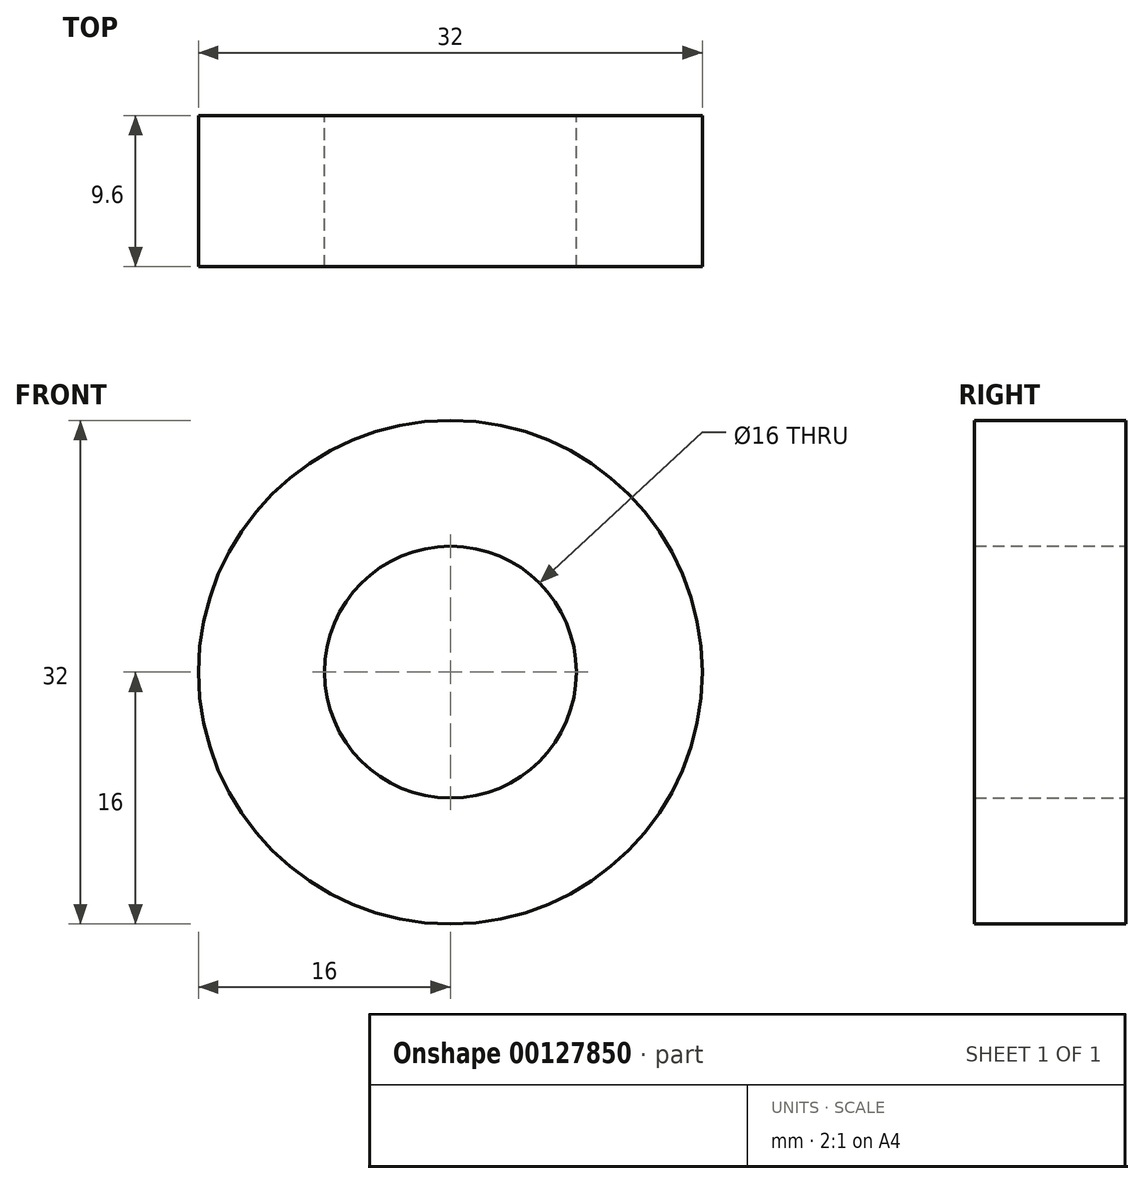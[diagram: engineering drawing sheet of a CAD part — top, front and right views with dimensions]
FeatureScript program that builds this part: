
annotation { "Feature Type Name" : "Feature", "Feature Type Description" : "" }
export const myFeature = defineFeature(function(context is Context, id is Id, definition is map)
    precondition{}
    {
        {
            var Q0;
            Q0=qCreatedBy(makeId("Front.planeOp"),FACE);
            var sketch = newSketch(context, id + "F0", { "sketchPlane" : qUnion([Q0])});
            skCircle(sketch, "E0", {"center": v(0, 0) * mm, "radius": 16 * mm});
            skCircle(sketch, "E1", {"center": v(0, 0) * mm, "radius": 8 * mm});
            skSolve(sketch);
        }
        {
            var Q0;
            Q0 = qSketchRegion(id + "FRdthEK2KyCKnt0_1", true);
            var Q1;
            Q1=makeQuery(id+"F0.imprint","IMPRINT",FACE,{"disambiguationData":[TD([[makeQuery(id+"F0.imprint","IMPRINT",EDGE,{"derivedFrom":sQuery(id+"F0.wireOp",EDGE,"E0")}),1.0]])]});
            extrude(context, id + "F1", {"entities" : qUnion([Q0, Q1]), "depth" : 9.6 * mm});
        }
    });
